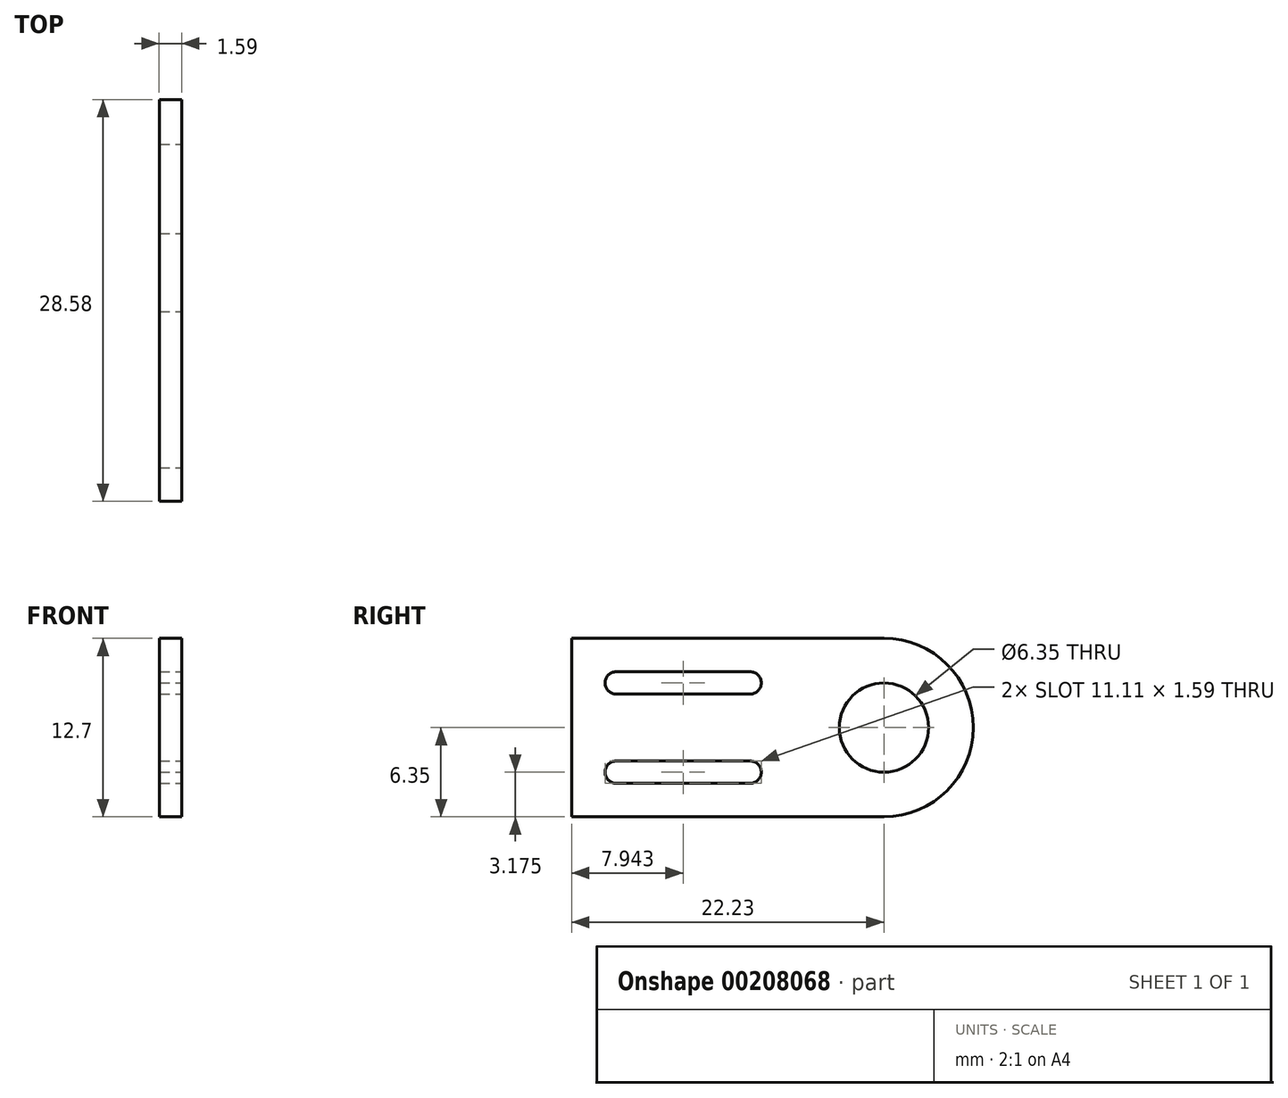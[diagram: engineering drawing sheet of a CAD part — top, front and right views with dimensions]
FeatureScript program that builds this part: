
annotation { "Feature Type Name" : "Feature", "Feature Type Description" : "" }
export const myFeature = defineFeature(function(context is Context, id is Id, definition is map)
    precondition{}
    {
        {
            var Q0;
            Q0=qCreatedBy(makeId("Right.planeOp"),FACE);
            var sketch = newSketch(context, id + "F0", { "sketchPlane" : qUnion([Q0])});
            skCircle(sketch, "E0", {"center": v(0, 0) * mm, "radius": 6.35 * mm});
            skCircle(sketch, "E1", {"center": v(0, 0) * mm, "radius": 3.18 * mm});
            skLineSegment(sketch, "E2.bottom", {"start": v(0, 6.35) * mm, "end": v(-22.23, 6.35) * mm});
            skLineSegment(sketch, "E2.top", {"start": v(0, -6.35) * mm, "end": v(-22.22, -6.35) * mm});
            skLineSegment(sketch, "E2.left", {"start": v(0, 6.35) * mm, "end": v(0, -6.35) * mm});
            skLineSegment(sketch, "E2.right", {"start": v(-22.23, 6.35) * mm, "end": v(-22.22, -6.35) * mm});
            skLineSegment(sketch, "E3", {"start": v(-27.41, 3.17) * mm, "end": v(-4.26, 3.17) * mm, "construction": true});
            skLineSegment(sketch, "E4", {"start": v(-4.26, 3.17) * mm, "end": v(-4.26, -3.17) * mm, "construction": true});
            skLineSegment(sketch, "E5", {"start": v(-4.26, -3.17) * mm, "end": v(-27.48, -3.18) * mm, "construction": true});
            skLineSegment(sketch, "E6", {"start": v(-19.05, 4.78) * mm, "end": v(-19.05, -4.75) * mm, "construction": true});
            skLineSegment(sketch, "E7", {"start": v(-19.05, -4.75) * mm, "end": v(-9.52, -4.75) * mm, "construction": true});
            skLineSegment(sketch, "E8", {"start": v(-9.52, -4.75) * mm, "end": v(-9.52, 4.82) * mm, "construction": true});
            skCircle(sketch, "E9", {"center": v(-19.05, 3.17) * mm, "radius": 0.8 * mm});
            skCircle(sketch, "E10", {"center": v(-9.52, 3.17) * mm, "radius": 0.8 * mm});
            skCircle(sketch, "E11", {"center": v(-9.52, -3.17) * mm, "radius": 0.8 * mm});
            skCircle(sketch, "E12", {"center": v(-19.05, -3.18) * mm, "radius": 0.8 * mm});
            skLineSegment(sketch, "E13", {"start": v(-19.05, 3.97) * mm, "end": v(-9.52, 3.97) * mm});
            skLineSegment(sketch, "E14", {"start": v(-19.05, 2.38) * mm, "end": v(-9.52, 2.38) * mm});
            skLineSegment(sketch, "E15", {"start": v(-19.05, -2.38) * mm, "end": v(-9.52, -2.38) * mm});
            skLineSegment(sketch, "E16", {"start": v(-19.05, -3.97) * mm, "end": v(-9.52, -3.97) * mm});
            skSolve(sketch);
        }
        {
            var Q0;
            Q0 = qSketchRegion(id + "F0", true);
            extrude(context, id + "F1", {"entities" : qUnion([Q0]), "oppositeDirection" : true, "depth" : 1.59 * mm});
        }
    });
